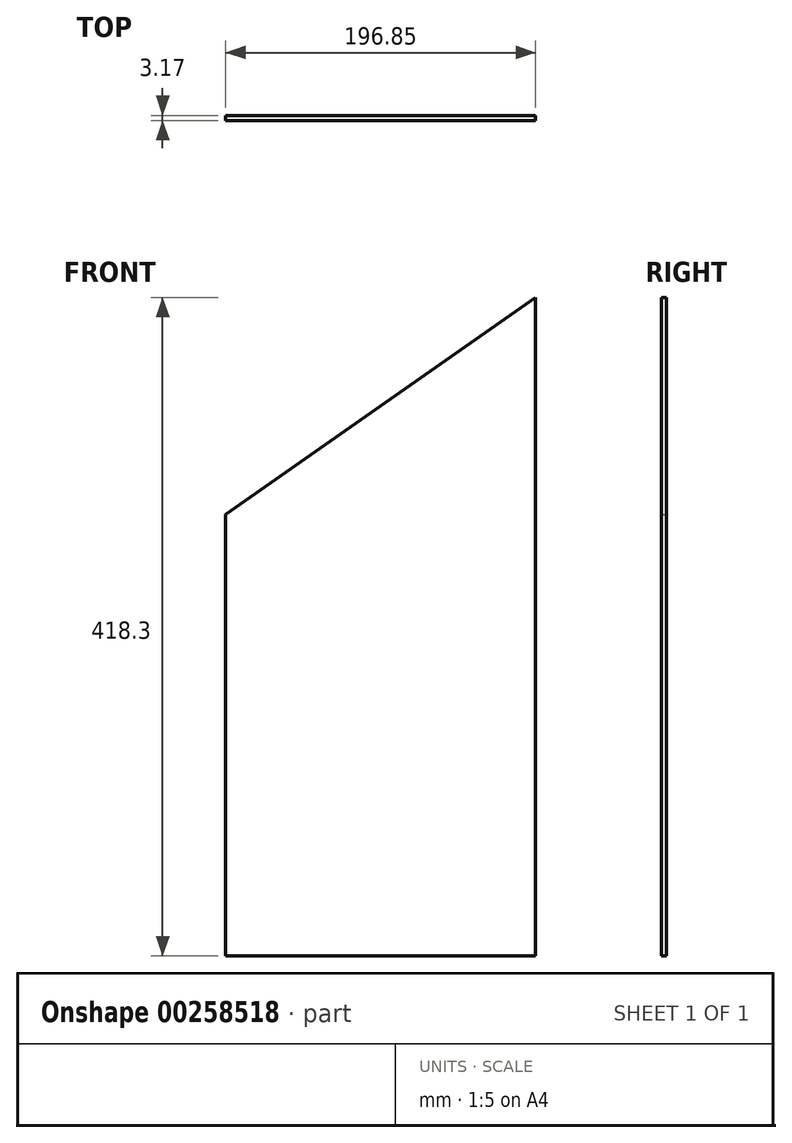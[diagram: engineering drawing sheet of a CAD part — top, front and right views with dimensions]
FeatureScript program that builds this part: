
annotation { "Feature Type Name" : "Feature", "Feature Type Description" : "" }
export const myFeature = defineFeature(function(context is Context, id is Id, definition is map)
    precondition{}
    {
        {
            var Q0;
            Q0=qCreatedBy(makeId("Front.planeOp"),FACE);
            var sketch = newSketch(context, id + "F0", { "sketchPlane" : qUnion([Q0])});
            skLineSegment(sketch, "E0.top", {"start": v(98.43, -209.15) * mm, "end": v(-98.43, -209.15) * mm});
            skLineSegment(sketch, "E0.left", {"start": v(98.43, 209.15) * mm, "end": v(98.42, -209.15) * mm});
            skLineSegment(sketch, "E0.right", {"start": v(-98.43, 71.31) * mm, "end": v(-98.43, -209.15) * mm});
            skPoint(sketch, "E0.middle", {"position": v(0, 0) * mm});
            skLineSegment(sketch, "E1", {"start": v(98.43, 209.15) * mm, "end": v(-98.42, 71.31) * mm});
            skPoint(sketch, "E2.orphan", {"position": v(-98.43, 209.15) * mm});
            skSolve(sketch);
        }
        {
            var Q0;
            Q0 = qSketchRegion(id + "F0", true);
            extrude(context, id + "F1", {"entities" : qUnion([Q0]), "depth" : 3.17 * mm});
        }
    });
